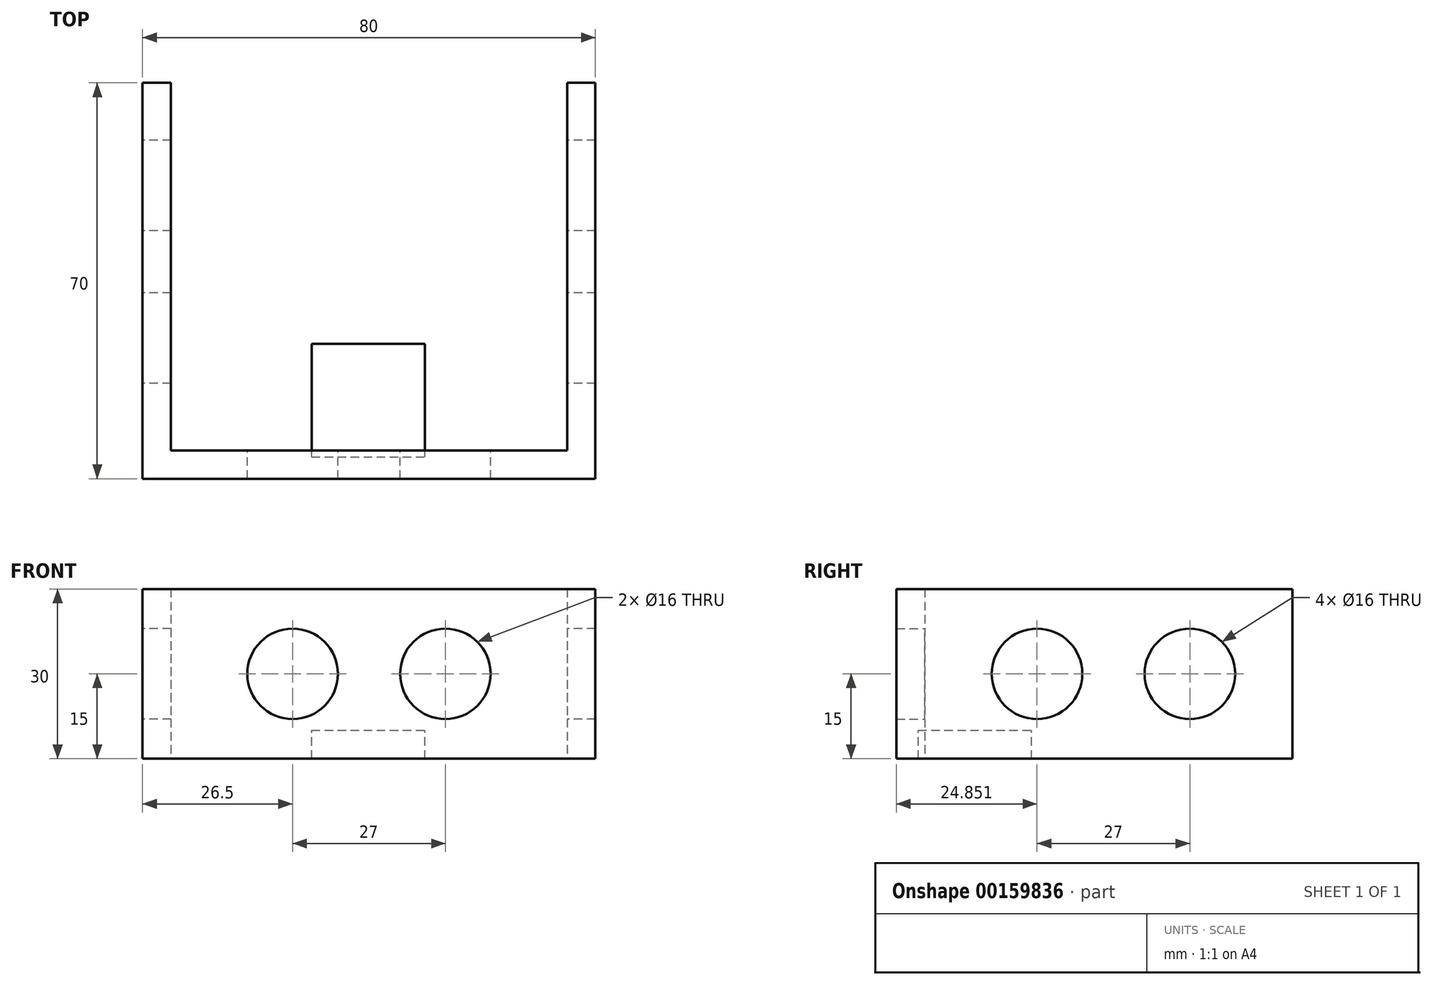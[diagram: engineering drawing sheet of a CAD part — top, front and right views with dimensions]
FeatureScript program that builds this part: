
annotation { "Feature Type Name" : "Feature", "Feature Type Description" : "" }
export const myFeature = defineFeature(function(context is Context, id is Id, definition is map)
    precondition{}
    {
        {
            var Q0;
            Q0=qCreatedBy(makeId("Top.planeOp"),FACE);
            var sketch = newSketch(context, id + "F0", { "sketchPlane" : qUnion([Q0])});
            skLineSegment(sketch, "E0.bottom", {"start": v(40, 2.5) * mm, "end": v(-40, 2.5) * mm});
            skLineSegment(sketch, "E0.top", {"start": v(40, -2.5) * mm, "end": v(-40, -2.5) * mm});
            skLineSegment(sketch, "E0.left", {"start": v(40, -2.5) * mm, "end": v(40, 2.5) * mm});
            skLineSegment(sketch, "E0.right", {"start": v(-40, -2.5) * mm, "end": v(-40, 2.5) * mm});
            skPoint(sketch, "E0.middle", {"position": v(0, 0) * mm});
            skLineSegment(sketch, "E1.bottom", {"start": v(-40, 2.5) * mm, "end": v(-35, 2.5) * mm});
            skLineSegment(sketch, "E1.top", {"start": v(-40, 67.5) * mm, "end": v(-35, 67.5) * mm});
            skLineSegment(sketch, "E1.left", {"start": v(-40, 2.5) * mm, "end": v(-40, 67.5) * mm});
            skLineSegment(sketch, "E1.right", {"start": v(-35, 2.5) * mm, "end": v(-35, 67.5) * mm});
            skLineSegment(sketch, "E2.bottom", {"start": v(40, 2.5) * mm, "end": v(35, 2.5) * mm});
            skLineSegment(sketch, "E2.top", {"start": v(40, 67.5) * mm, "end": v(35, 67.5) * mm});
            skLineSegment(sketch, "E2.left", {"start": v(40, 2.5) * mm, "end": v(40, 67.5) * mm});
            skLineSegment(sketch, "E2.right", {"start": v(35, 2.5) * mm, "end": v(35, 67.5) * mm});
            skSolve(sketch);
        }
        {
            var Q0;
            Q0 = qSketchRegion(id + "F0", true);
            extrude(context, id + "F1", {"entities" : qUnion([Q0]), "endBound" : BoundingType.SYMMETRIC, "depth" : 30 * mm});
        }
        {
            var Q0;
            Q0=qCreatedBy(makeId("Front.planeOp"),FACE);
            var sketch = newSketch(context, id + "F2", { "sketchPlane" : qUnion([Q0])});
            skCircle(sketch, "E3", {"center": v(-13.5, 0) * mm, "radius": 8 * mm});
            skCircle(sketch, "E4", {"center": v(13.5, 0) * mm, "radius": 8 * mm});
            skLineSegment(sketch, "E5", {"start": v(-13.5, 0) * mm, "end": v(0, 0) * mm});
            skLineSegment(sketch, "E6", {"start": v(0, 0) * mm, "end": v(13.5, 0) * mm});
            skSolve(sketch);
        }
        {
            var Q0;
            Q0 = qSketchRegion(id + "F2", true);
            extrude(context, id + "F3", {"entities" : qUnion([Q0]), "endBound" : BoundingType.SYMMETRIC, "depth" : 25 * mm});
        }
        {
            var Q0;
            Q0=makeQuery(id+"F3.opExtrude","SWEPT_BODY",BODY,{"disambiguationData":[OSD([sQuery(id+"F2.wireOp",EDGE,"E3")])]});
            var Q1;
            Q1=makeQuery(id+"F3.opExtrude","SWEPT_BODY",BODY,{"disambiguationData":[OSD([sQuery(id+"F2.wireOp",EDGE,"E4")])]});
            var Q2;
            Q2=makeQuery(id+"F1.opExtrude","SWEPT_BODY",BODY,{"disambiguationData":[OSD([sQuery(id+"F0.wireOp",EDGE,"E0.bottom"),sQuery(id+"F0.wireOp",EDGE,"E0.top"),sQuery(id+"F0.wireOp",EDGE,"E0.left"),sQuery(id+"F0.wireOp",EDGE,"E0.right"),sQuery(id+"F0.wireOp",EDGE,"E1.top"),sQuery(id+"F0.wireOp",EDGE,"E1.left"),sQuery(id+"F0.wireOp",EDGE,"E1.right"),sQuery(id+"F0.wireOp",EDGE,"E2.top"),sQuery(id+"F0.wireOp",EDGE,"E2.left"),sQuery(id+"F0.wireOp",EDGE,"E2.right")])]});
            booleanBodies(context, id + "F4", {"operationType" : BooleanOperationType.SUBTRACTION, "tools" : qUnion([Q0, Q1]), "targets" : qUnion([Q2])});
        }
        {
            var Q0;
            Q0=qCreatedBy(makeId("Right.planeOp"),FACE);
            var sketch = newSketch(context, id + "F5", { "sketchPlane" : qUnion([Q0])});
            skCircle(sketch, "E7", {"center": v(22.35, 0) * mm, "radius": 8 * mm});
            skCircle(sketch, "E8", {"center": v(49.35, 0) * mm, "radius": 8 * mm});
            skLineSegment(sketch, "E9", {"start": v(2.35, 0) * mm, "end": v(22.35, 0) * mm});
            skLineSegment(sketch, "E10", {"start": v(22.35, 0) * mm, "end": v(49.35, 0) * mm});
            skSolve(sketch);
        }
        {
            var Q0;
            Q0 = qSketchRegion(id + "F5", true);
            extrude(context, id + "F6", {"entities" : qUnion([Q0]), "endBound" : BoundingType.SYMMETRIC, "depth" : 100 * mm});
        }
        {
            var Q0;
            Q0=makeQuery(id+"F6.opExtrude","SWEPT_BODY",BODY,{"disambiguationData":[OSD([sQuery(id+"F5.wireOp",EDGE,"E7")])]});
            var Q1;
            Q1=makeQuery(id+"F6.opExtrude","SWEPT_BODY",BODY,{"disambiguationData":[OSD([sQuery(id+"F5.wireOp",EDGE,"E8")])]});
            var Q2;
            Q2=makeQuery(id+"F1.opExtrude","SWEPT_BODY",BODY,{"disambiguationData":[OSD([sQuery(id+"F0.wireOp",EDGE,"E0.bottom"),sQuery(id+"F0.wireOp",EDGE,"E0.top"),sQuery(id+"F0.wireOp",EDGE,"E0.left"),sQuery(id+"F0.wireOp",EDGE,"E0.right"),sQuery(id+"F0.wireOp",EDGE,"E1.top"),sQuery(id+"F0.wireOp",EDGE,"E1.left"),sQuery(id+"F0.wireOp",EDGE,"E1.right"),sQuery(id+"F0.wireOp",EDGE,"E2.top"),sQuery(id+"F0.wireOp",EDGE,"E2.left"),sQuery(id+"F0.wireOp",EDGE,"E2.right")])]});
            booleanBodies(context, id + "F7", {"operationType" : BooleanOperationType.SUBTRACTION, "tools" : qUnion([Q0, Q1]), "targets" : qUnion([Q2])});
        }
        {
            var Q0;
            Q0=qCreatedBy(makeId("Top.planeOp"),FACE);
            var sketch = newSketch(context, id + "F8", { "sketchPlane" : qUnion([Q0])});
            skLineSegment(sketch, "E11.bottom", {"start": v(-10.13, 1.36) * mm, "end": v(9.87, 1.36) * mm});
            skLineSegment(sketch, "E11.top", {"start": v(-10.13, 21.36) * mm, "end": v(9.87, 21.36) * mm});
            skLineSegment(sketch, "E11.left", {"start": v(-10.13, 1.36) * mm, "end": v(-10.13, 21.36) * mm});
            skLineSegment(sketch, "E11.right", {"start": v(9.87, 1.36) * mm, "end": v(9.87, 21.36) * mm});
            skLineSegment(sketch, "E12", {"start": v(0, 0) * mm, "end": v(-10, 0) * mm});
            skSolve(sketch);
        }
        {
            var Q0;
            Q0 = qSketchRegion(id + "F8", true);
            extrude(context, id + "F9", {"entities" : qUnion([Q0]), "oppositeDirection" : true, "depth" : 15 * mm, "hasSecondDirection" : true, "secondDirectionOppositeDirection" : true, "secondDirectionDepth" : 10 * mm});
        }
    });
